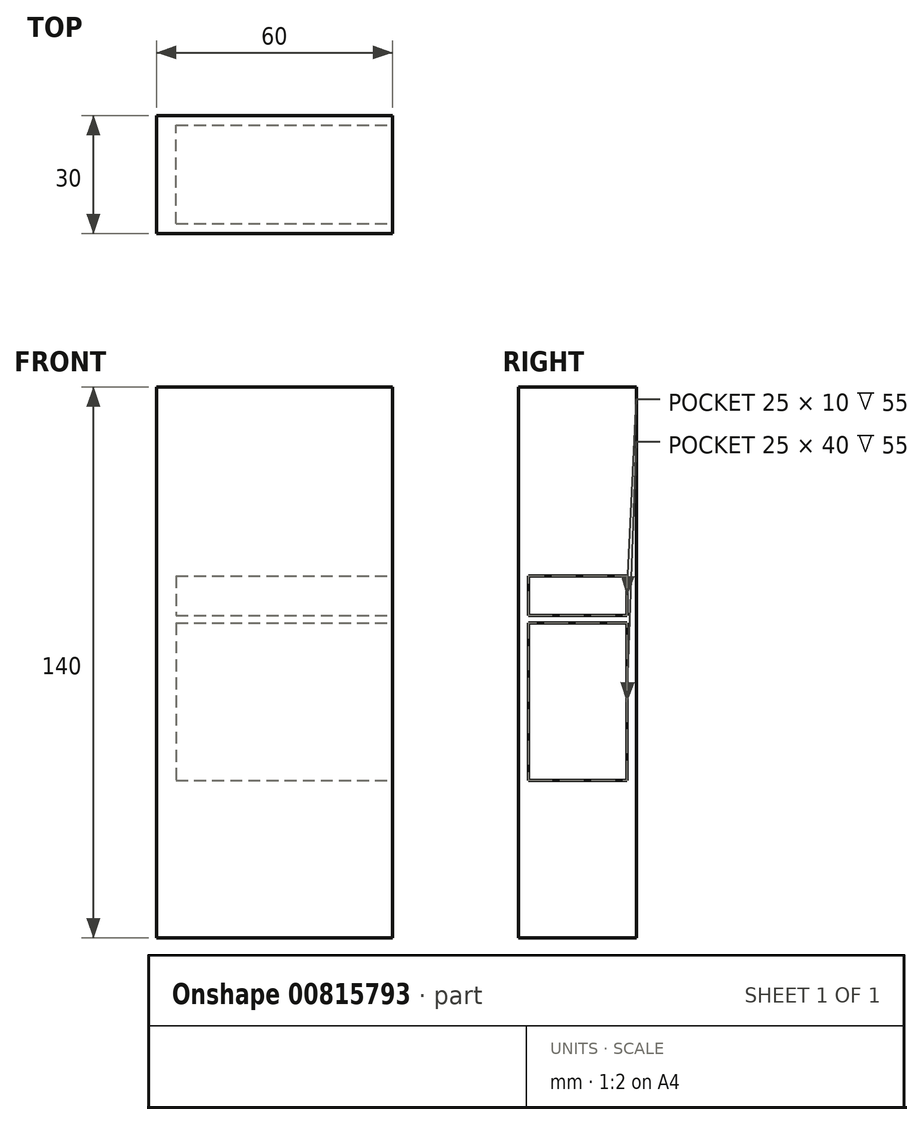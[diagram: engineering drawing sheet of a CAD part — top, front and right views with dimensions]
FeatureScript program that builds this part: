
annotation { "Feature Type Name" : "Feature", "Feature Type Description" : "" }
export const myFeature = defineFeature(function(context is Context, id is Id, definition is map)
    precondition{}
    {
        {
            var Q0;
            Q0=qCreatedBy(makeId("Front.planeOp"),FACE);
            var sketch = newSketch(context, id + "F0", { "sketchPlane" : qUnion([Q0])});
            skLineSegment(sketch, "E0.bottom", {"start": v(0, 0) * mm, "end": v(60, 0) * mm});
            skLineSegment(sketch, "E0.top", {"start": v(0, 140) * mm, "end": v(60, 140) * mm});
            skLineSegment(sketch, "E0.left", {"start": v(0, 0) * mm, "end": v(0, 140) * mm});
            skLineSegment(sketch, "E0.right", {"start": v(60, 0) * mm, "end": v(60, 140) * mm});
            skSolve(sketch);
        }
        {
            var Q0;
            Q0 = qSketchRegion(id + "F0", true);
            extrude(context, id + "F1", {"entities" : qUnion([Q0]), "depth" : 30 * mm, "offsetDistance" : 25 * mm});
        }
        {
            var Q0;
            Q0=makeQuery(id+"F1.opExtrude","SWEPT_FACE",FACE,{"disambiguationData":[OSD([sQuery(id+"F0.wireOp",EDGE,"E0.right")])]});
            var sketch = newSketch(context, id + "F2", { "sketchPlane" : qUnion([Q0])});
            skLineSegment(sketch, "E1.bottom", {"start": v(-27.5, 80) * mm, "end": v(-2.5, 80) * mm});
            skLineSegment(sketch, "E1.top", {"start": v(-27.5, 40) * mm, "end": v(-2.5, 40) * mm});
            skLineSegment(sketch, "E1.left", {"start": v(-27.5, 80) * mm, "end": v(-27.5, 40) * mm});
            skLineSegment(sketch, "E1.right", {"start": v(-2.5, 80) * mm, "end": v(-2.5, 40) * mm});
            skLineSegment(sketch, "E2.bottom", {"start": v(-27.5, 92) * mm, "end": v(-2.5, 92) * mm});
            skLineSegment(sketch, "E2.top", {"start": v(-27.5, 82) * mm, "end": v(-2.5, 82) * mm});
            skLineSegment(sketch, "E2.left", {"start": v(-27.5, 92) * mm, "end": v(-27.5, 82) * mm});
            skLineSegment(sketch, "E2.right", {"start": v(-2.5, 92) * mm, "end": v(-2.5, 82) * mm});
            skSolve(sketch);
        }
        {
            var Q0;
            Q0 = qSketchRegion(id + "F2", true);
            extrude(context, id + "F3", {"entities" : qUnion([Q0]), "operationType" : NewBodyOperationType.REMOVE, "oppositeDirection" : true, "depth" : 55 * mm, "offsetDistance" : 25 * mm});
        }
    });
